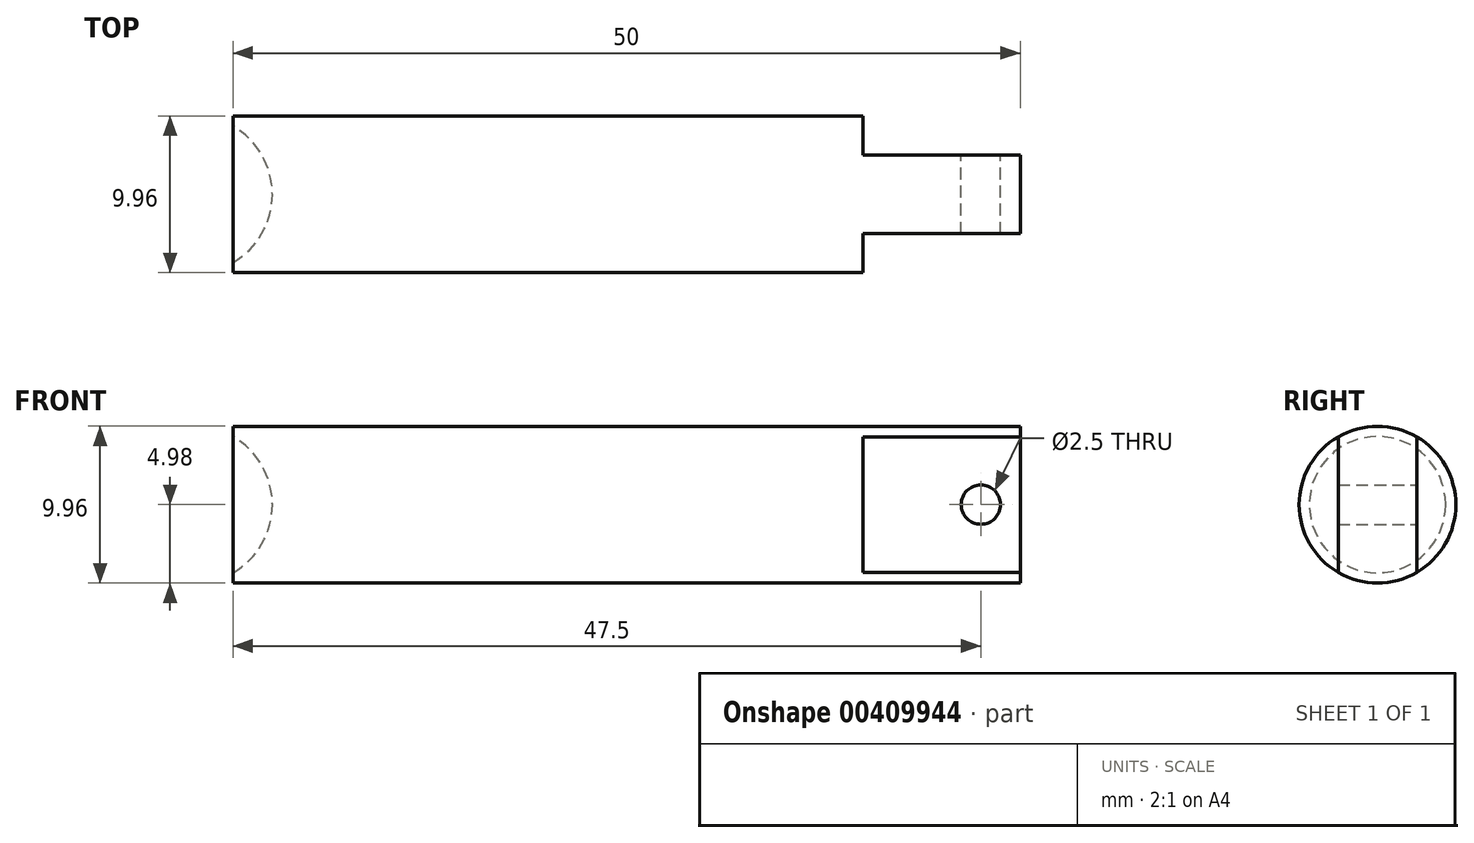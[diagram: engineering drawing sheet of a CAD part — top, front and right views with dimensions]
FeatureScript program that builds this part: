
annotation { "Feature Type Name" : "Feature", "Feature Type Description" : "" }
export const myFeature = defineFeature(function(context is Context, id is Id, definition is map)
    precondition{}
    {
        {
            var Q0;
            Q0=qCreatedBy(makeId("Right.planeOp"),FACE);
            var sketch = newSketch(context, id + "F0", { "sketchPlane" : qUnion([Q0])});
            skCircle(sketch, "E0", {"center": v(0, 0) * mm, "radius": 4.98 * mm});
            skSolve(sketch);
        }
        {
            var Q0;
            Q0=makeQuery(id+"F0.imprint","IMPRINT",FACE,{"disambiguationData":[TD([[makeQuery(id+"F0.imprint","IMPRINT",EDGE,{"derivedFrom":sQuery(id+"F0.wireOp",EDGE,"E0")}),1.0]])]});
            extrude(context, id + "F1", {"entities" : qUnion([Q0]), "depth" : 50 * mm});
        }
        {
            var Q0;
            Q0=makeQuery(id+"F1.opExtrude","CAP_FACE",FACE,{"disambiguationData":[OSD([sQuery(id+"F0.wireOp",EDGE,"E0")])],"isStart":false});
            var sketch = newSketch(context, id + "F2", { "sketchPlane" : qUnion([Q0])});
            skLineSegment(sketch, "E1", {"start": v(-2.5, -4.3) * mm, "end": v(-2.5, 4.3) * mm});
            skLineSegment(sketch, "E2", {"start": v(2.5, -4.3) * mm, "end": v(2.5, 4.3) * mm});
            skArc(sketch, "E3", {"start": v(-2.5, 4.3) * mm, "mid": v(-4.98, 0) * mm, "end": v(-2.5, -4.3) * mm});
            skArc(sketch, "E4.trimOffspring", {"start": v(2.5, -4.3) * mm, "mid": v(4.98, 0) * mm, "end": v(2.5, 4.3) * mm});
            skSolve(sketch);
        }
        {
            var Q0;
            Q0=makeQuery(id+"F2.imprint","IMPRINT",FACE,{"disambiguationData":[TD([[makeQuery(id+"F2.imprint","IMPRINT",EDGE,{"derivedFrom":sQuery(id+"F2.wireOp",EDGE,"E2")}),-1.0]])]});
            var Q1;
            Q1=makeQuery(id+"F2.imprint","IMPRINT",FACE,{"disambiguationData":[TD([[makeQuery(id+"F2.imprint","IMPRINT",EDGE,{"derivedFrom":sQuery(id+"F2.wireOp",EDGE,"E1")}),1.0]])]});
            extrude(context, id + "F3", {"entities" : qUnion([Q0, Q1]), "operationType" : NewBodyOperationType.REMOVE, "oppositeDirection" : true, "depth" : 10 * mm});
        }
        {
            var Q0;
            Q0=makeQuery(id+"F3.boolean.opBoolean","COPY",FACE,{"derivedFrom":makeQuery(id+"F3.opExtrude","SWEPT_FACE",FACE,{"disambiguationData":[OSD([sQuery(id+"F2.wireOp",EDGE,"E2")])]})});
            var sketch = newSketch(context, id + "F4", { "sketchPlane" : qUnion([Q0])});
            skCircle(sketch, "E5", {"center": v(-47.5, 0) * mm, "radius": 1.25 * mm});
            skPoint(sketch, "E5.centerSnap0", {"position": v(-50, 0) * mm});
            skSolve(sketch);
        }
        {
            var Q0;
            Q0=makeQuery(id+"F4.imprint","IMPRINT",FACE,{"disambiguationData":[TD([[makeQuery(id+"F4.imprint","IMPRINT",EDGE,{"derivedFrom":sQuery(id+"F4.wireOp",EDGE,"E5")}),1.0]])]});
            extrude(context, id + "F5", {"entities" : qUnion([Q0]), "operationType" : NewBodyOperationType.REMOVE, "oppositeDirection" : true, "depth" : 5 * mm});
        }
        {
            var Q0;
            Q0=qCreatedBy(makeId("Front.planeOp"),FACE);
            var sketch = newSketch(context, id + "F6", { "sketchPlane" : qUnion([Q0])});
            skArc(sketch, "E6", {"start": v(-2.5, -5) * mm, "mid": v(2.5, 0) * mm, "end": v(-2.5, 5) * mm});
            skLineSegment(sketch, "E7", {"start": v(-2.5, -5) * mm, "end": v(-2.5, 5) * mm});
            skSolve(sketch);
        }
        {
            var Q0;
            Q0=makeQuery(id+"F6.imprint","IMPRINT",FACE,{"disambiguationData":[TD([[makeQuery(id+"F6.imprint","IMPRINT",EDGE,{"derivedFrom":sQuery(id+"F6.wireOp",EDGE,"E6")}),1.0]])]});
            var Q1;
            Q1=sQuery(id+"F6.wireOp",EDGE,"E7");
            revolve(context, id + "F7", {"operationType" : NewBodyOperationType.REMOVE, "entities" : qUnion([Q0]), "axis" : qUnion([Q1]), "revolveType" : RevolveType.FULL, "oppositeDirection" : true});
        }
    });
